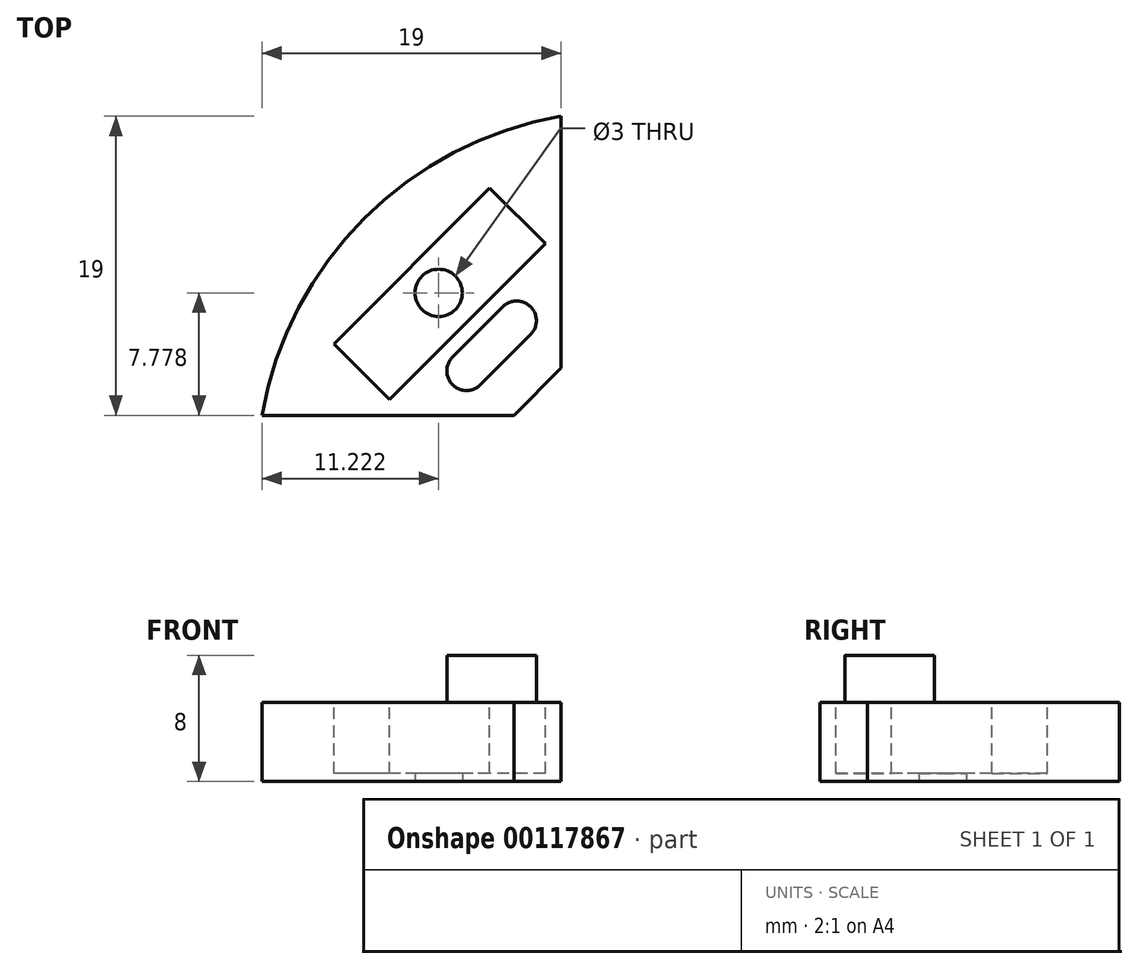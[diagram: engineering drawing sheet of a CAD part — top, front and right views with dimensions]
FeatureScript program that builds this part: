
annotation { "Feature Type Name" : "Feature", "Feature Type Description" : "" }
export const myFeature = defineFeature(function(context is Context, id is Id, definition is map)
    precondition{}
    {
        {
            var Q0;
            Q0=qCreatedBy(makeId("Top.planeOp"),FACE);
            var sketch = newSketch(context, id + "F0", { "sketchPlane" : qUnion([Q0])});
            skLineSegment(sketch, "E0", {"start": v(0, 3) * mm, "end": v(0, 19) * mm});
            skLineSegment(sketch, "E1", {"start": v(-3, 0) * mm, "end": v(-19, 0) * mm});
            skArc(sketch, "E2", {"start": v(0, 19) * mm, "mid": v(-12.51, 12.51) * mm, "end": v(-19, 0) * mm});
            skPoint(sketch, "E3.visualSharp", {"position": v(0, 0) * mm});
            skLineSegment(sketch, "E4", {"start": v(-3, 0) * mm, "end": v(0, 3) * mm});
            skSolve(sketch);
        }
        {
            var Q0;
            Q0=makeQuery(id+"F0.imprint","IMPRINT",FACE,{"disambiguationData":[TD([[makeQuery(id+"F0.imprint","IMPRINT",EDGE,{"derivedFrom":sQuery(id+"F0.wireOp",EDGE,"E0")}),1.0]])]});
            extrude(context, id + "F1", {"entities" : qUnion([Q0]), "depth" : 5 * mm});
        }
        {
            var Q0;
            Q0=makeQuery(id+"F1.opExtrude","CAP_FACE",FACE,{"disambiguationData":[OSD([sQuery(id+"F0.wireOp",EDGE,"E0"),sQuery(id+"F0.wireOp",EDGE,"E1"),sQuery(id+"F0.wireOp",EDGE,"E2"),sQuery(id+"F0.wireOp",EDGE,"E3.filletArc")])],"isStart":false});
            var sketch = newSketch(context, id + "F2", { "sketchPlane" : qUnion([Q0])});
            skLineSegment(sketch, "E5.bottom", {"start": v(-1, 10.9) * mm, "end": v(-10.9, 1) * mm});
            skLineSegment(sketch, "E5.top", {"start": v(-4.54, 14.44) * mm, "end": v(-14.44, 4.54) * mm});
            skLineSegment(sketch, "E5.left", {"start": v(-1, 10.9) * mm, "end": v(-4.54, 14.44) * mm});
            skLineSegment(sketch, "E5.right", {"start": v(-10.9, 1) * mm, "end": v(-14.44, 4.54) * mm});
            skSolve(sketch);
        }
        {
            var Q0;
            Q0=makeQuery(id+"F2.imprint","IMPRINT",FACE,{"disambiguationData":[TD([[makeQuery(id+"F2.imprint","IMPRINT",EDGE,{"derivedFrom":sQuery(id+"F2.wireOp",EDGE,"E5.bottom")}),-1.0]])]});
            extrude(context, id + "F3", {"entities" : qUnion([Q0]), "operationType" : NewBodyOperationType.REMOVE, "oppositeDirection" : true, "depth" : 4.5 * mm});
        }
        {
            var Q0;
            Q0=makeQuery(id+"F2.imprint","IMPRINT",FACE,{"disambiguationData":[TD([[makeQuery(id+"F2.imprint","IMPRINT",EDGE,{"derivedFrom":sQuery(id+"F2.wireOp",EDGE,"E5.bottom")}),1.0]])]});
            var sketch = newSketch(context, id + "F4", { "sketchPlane" : qUnion([Q0])});
            skLineSegment(sketch, "E6", {"start": v(-6.9, 3.71) * mm, "end": v(-3.71, 6.9) * mm});
            skLineSegment(sketch, "E7", {"start": v(-1.94, 5.13) * mm, "end": v(-5.13, 1.94) * mm});
            skArc(sketch, "E8", {"start": v(-6.9, 3.71) * mm, "mid": v(-6.9, 1.94) * mm, "end": v(-5.13, 1.94) * mm});
            skArc(sketch, "E9", {"start": v(-1.94, 5.13) * mm, "mid": v(-1.95, 6.9) * mm, "end": v(-3.71, 6.9) * mm});
            skLineSegment(sketch, "E10", {"start": v(-3.54, 3.54) * mm, "end": v(3.35, -3.35) * mm, "construction": true});
            skSolve(sketch);
        }
        {
            var Q0;
            Q0 = qSketchRegion(id + "F4", true);
            extrude(context, id + "F5", {"entities" : qUnion([Q0]), "operationType" : NewBodyOperationType.ADD, "depth" : 3 * mm});
        }
        {
            var Q0;
            Q0=makeQuery(id+"F0.imprint","IMPRINT",FACE,{"disambiguationData":[TD([[makeQuery(id+"F0.imprint","IMPRINT",EDGE,{"derivedFrom":sQuery(id+"F0.wireOp",EDGE,"E0")}),1.0]])]});
            var sketch = newSketch(context, id + "F6", { "sketchPlane" : qUnion([Q0])});
            skCircle(sketch, "E11", {"center": v(-7.78, 7.78) * mm, "radius": 1.5 * mm});
            skSolve(sketch);
        }
        {
            var Q0;
            Q0 = qSketchRegion(id + "F6", true);
            extrude(context, id + "F7", {"entities" : qUnion([Q0]), "operationType" : NewBodyOperationType.REMOVE, "endBound" : BoundingType.THROUGH_ALL, "depth" : 25.4 * mm});
        }
    });
